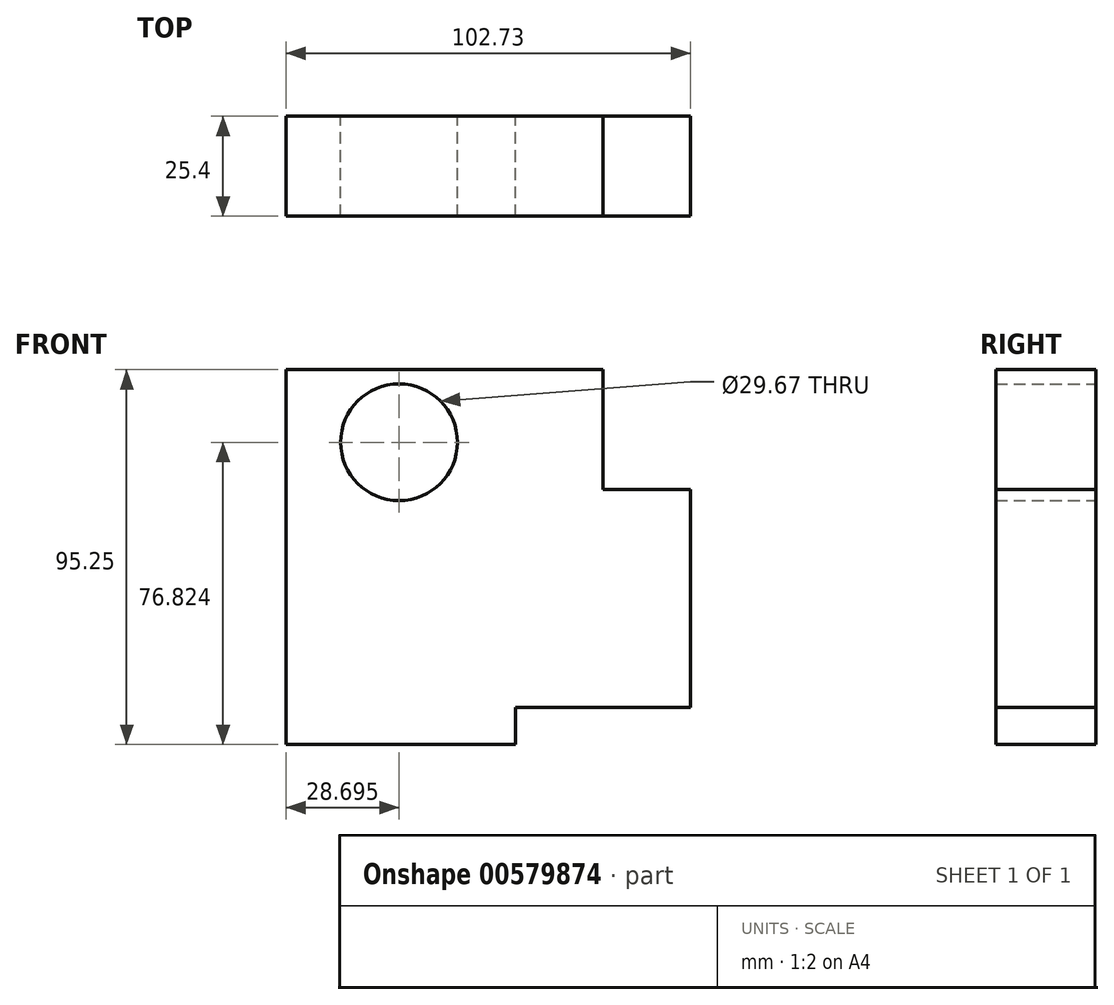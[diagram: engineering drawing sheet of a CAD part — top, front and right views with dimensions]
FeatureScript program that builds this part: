
annotation { "Feature Type Name" : "Feature", "Feature Type Description" : "" }
export const myFeature = defineFeature(function(context is Context, id is Id, definition is map)
    precondition{}
    {
        {
            var Q0;
            Q0=qCreatedBy(makeId("Front.planeOp"),FACE);
            var sketch = newSketch(context, id + "F0", { "sketchPlane" : qUnion([Q0])});
            skLineSegment(sketch, "E0.bottom", {"start": v(-118.53, 60.3) * mm, "end": v(-60.3, 60.3) * mm});
            skLineSegment(sketch, "E0.top", {"start": v(-118.53, -34.94) * mm, "end": v(-60.3, -34.94) * mm});
            skLineSegment(sketch, "E0.left", {"start": v(-118.53, 60.3) * mm, "end": v(-118.53, -34.94) * mm});
            skLineSegment(sketch, "E0.right", {"start": v(-60.3, 60.3) * mm, "end": v(-60.3, -34.94) * mm});
            skLineSegment(sketch, "E1", {"start": v(-60.3, 29.93) * mm, "end": v(-15.8, 29.93) * mm});
            skLineSegment(sketch, "E2", {"start": v(-15.8, 29.93) * mm, "end": v(-15.8, -25.5) * mm});
            skLineSegment(sketch, "E3", {"start": v(-15.8, -25.5) * mm, "end": v(-60.3, -25.5) * mm});
            skLineSegment(sketch, "E4", {"start": v(-60.3, 60.3) * mm, "end": v(-38.08, 60.3) * mm});
            skLineSegment(sketch, "E5", {"start": v(-38.08, 60.3) * mm, "end": v(-38.08, 29.93) * mm});
            skSolve(sketch);
        }
        {
            var Q0;
            {var subQ1=sQuery(id+"F0.wireOp",EDGE,"E0.bottom");Q0=makeQuery(id+"F0.imprint","IMPRINT",FACE,{"disambiguationData":[TD([[makeQuery(id+"F0.imprint","IMPRINT",EDGE,{"derivedFrom":subQ1}),-1.0]])]});}
            var Q1;
            {var subQ0=sQuery(id+"F0.wireOp",EDGE,"E2");Q1=makeQuery(id+"F0.imprint","IMPRINT",FACE,{"disambiguationData":[TD([[makeQuery(id+"F0.imprint","IMPRINT",EDGE,{"derivedFrom":subQ0}),-1.0]])]});}
            var Q2;
            {var subQ0=sQuery(id+"F0.wireOp",EDGE,"E4");Q2=makeQuery(id+"F0.imprint","IMPRINT",FACE,{"disambiguationData":[TD([[makeQuery(id+"F0.imprint","IMPRINT",EDGE,{"derivedFrom":subQ0}),-1.0]])]});}
            extrude(context, id + "F1", {"entities" : qUnion([Q0, Q1, Q2]), "depth" : 25.4 * mm, "offsetDistance" : 25.4 * mm});
        }
        {
            var Q0;
            Q0=qCreatedBy(makeId("Front.planeOp"),FACE);
            var sketch = newSketch(context, id + "F2", { "sketchPlane" : qUnion([Q0])});
            skCircle(sketch, "E6", {"center": v(-89.83, 41.88) * mm, "radius": 14.83 * mm});
            skSolve(sketch);
        }
        {
            var Q0;
            Q0=makeQuery(id+"F2.imprint","IMPRINT",FACE,{"disambiguationData":[TD([[makeQuery(id+"F2.imprint","IMPRINT",EDGE,{"derivedFrom":sQuery(id+"F2.wireOp",EDGE,"E6")}),1.0]])]});
            extrude(context, id + "F3", {"entities" : qUnion([Q0]), "operationType" : NewBodyOperationType.REMOVE, "endBound" : BoundingType.THROUGH_ALL, "depth" : 25.4 * mm, "offsetDistance" : 25.4 * mm});
        }
    });
